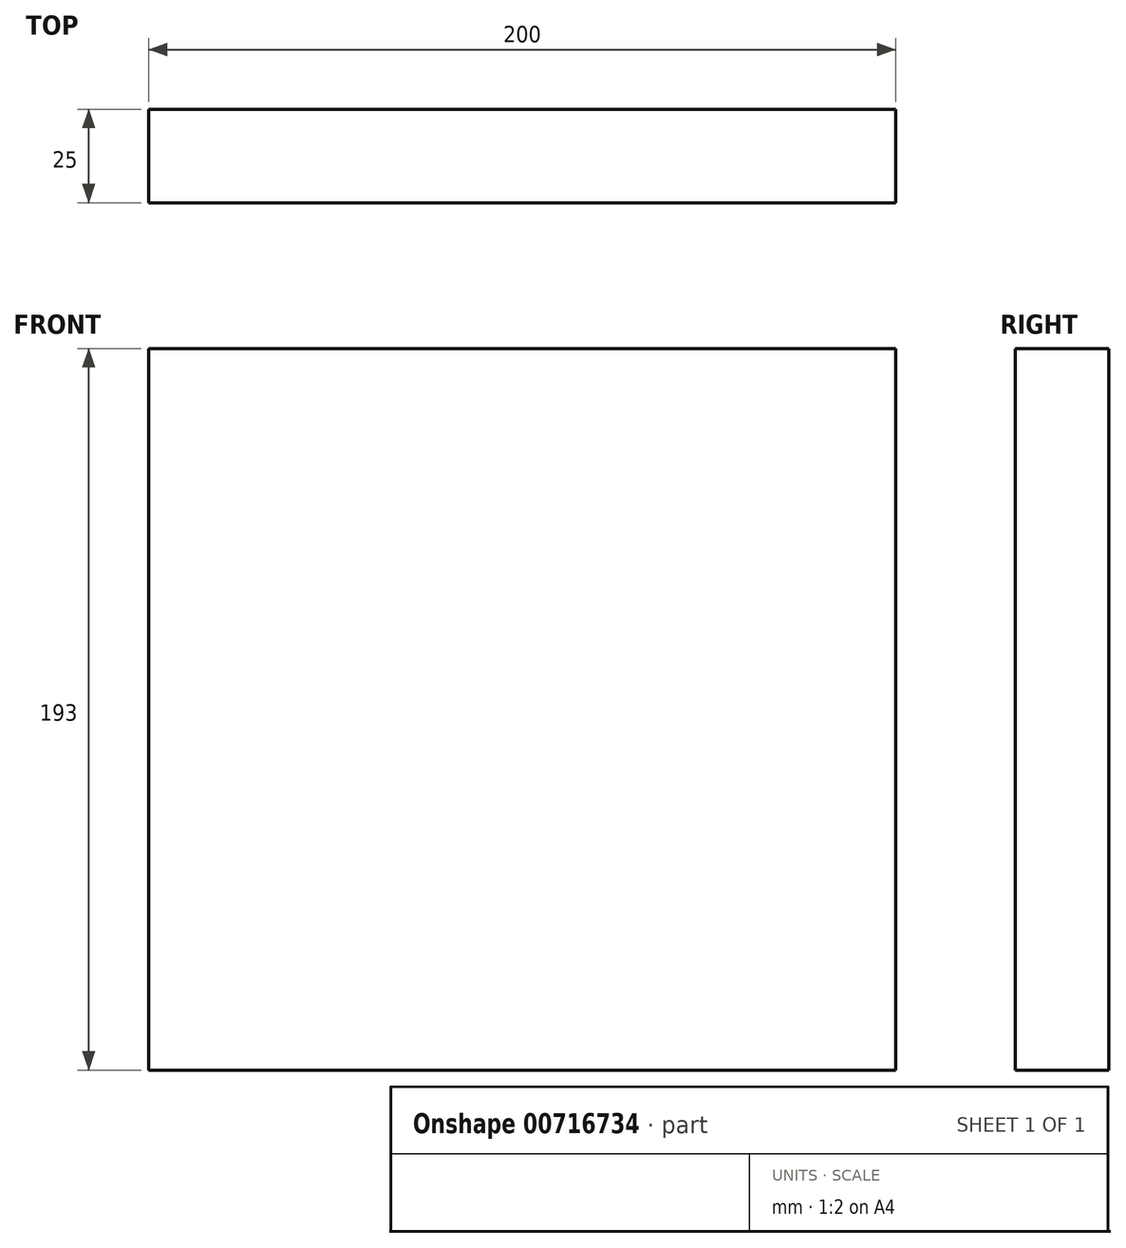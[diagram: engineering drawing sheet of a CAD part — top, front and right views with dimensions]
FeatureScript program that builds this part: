
annotation { "Feature Type Name" : "Feature", "Feature Type Description" : "" }
export const myFeature = defineFeature(function(context is Context, id is Id, definition is map)
    precondition{}
    {
        {
            var Q0;
            Q0=qCreatedBy(makeId("Front.planeOp"),FACE);
            var sketch = newSketch(context, id + "F0", { "sketchPlane" : qUnion([Q0])});
            skLineSegment(sketch, "E0.bottom", {"start": v(-100.8, 115.38) * mm, "end": v(99.2, 115.38) * mm});
            skLineSegment(sketch, "E0.top", {"start": v(-100.8, -77.62) * mm, "end": v(99.2, -77.62) * mm});
            skLineSegment(sketch, "E0.left", {"start": v(-100.8, 115.38) * mm, "end": v(-100.8, -77.62) * mm});
            skLineSegment(sketch, "E0.right", {"start": v(99.2, 115.38) * mm, "end": v(99.2, -77.62) * mm});
            skSolve(sketch);
        }
        {
            var Q0;
            Q0=makeQuery(id+"F0.imprint","IMPRINT",FACE,{"disambiguationData":[TD([[makeQuery(id+"F0.imprint","IMPRINT",EDGE,{"derivedFrom":sQuery(id+"F0.wireOp",EDGE,"E0.bottom")}),-1.0]])]});
            extrude(context, id + "F1", {"entities" : qUnion([Q0]), "depth" : 25 * mm, "offsetDistance" : 25 * mm});
        }
    });
